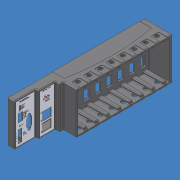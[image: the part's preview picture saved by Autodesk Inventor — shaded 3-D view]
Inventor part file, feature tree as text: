
AUTODESK INVENTOR PART (.ipt)
format: ipt  version: 2011 (Build 150239000, 239)  size: 1,395,712 bytes
history: native  units: mm (DEFAULTED — no unit token found)
features: sketch x25, extrude x19, pattern_linear x9, fillet x7, hole x4, mirror x2, other x2
ambient origin geometry x8: Origin, YZ Plane, XZ Plane, XY Plane, X Axis, Y Axis, Z Axis, Center Point
bodies: Solid1 (feature_tree)
feature tree (68):
  extrude  "Extrusion1"  Depth=15.494mm
  extrude  "Extrusion2"  Depth=58.928mm
  extrude  "Extrusion3"  Depth=44.45mm
  extrude  "Extrusion4"  Depth=34.29mm
  extrude  "Extrusion5"  Depth=278.8412mm
  hole  "Hole2"  [1 undecoded]
  mirror  "Mirror2"
  pattern_linear  "Rectangular Pattern1"  Count1=2 Spacing1=93.0148mm
  pattern_linear  "Rectangular Pattern2"  Count1=2 Spacing1=140.589mm
  pattern_linear  "Rectangular Pattern3"  Count1=2 Spacing1=235.077mm
  pattern_linear  "Rectangular Pattern5"  Count1=2 Spacing1=81.534mm
  hole  "Hole3"  [1 undecoded]
  extrude  "Extrusion6"  Depth=11.1125mm
  extrude  "Extrusion7"  Depth=15.875mm
  extrude  "Extrusion8"  Depth=9.8298mm
  pattern_linear  "Rectangular Pattern6"  Count1=2 Spacing1=165.1mm
  extrude  "Extrusion9"  Depth=20.32mm
  pattern_linear  "Rectangular Pattern7"  Spacing1=5.08mm  [1 undecoded]
  extrude  "Extrusion10"  Depth=6.35mm
  extrude  "Extrusion11"  Depth=1.905mm
  extrude  "Extrusion12"  Depth=3.175mm TaperAngle=0.0deg
  extrude  "Extrusion13"  Depth=80.0mm
  extrude  "Extrusion14"  Depth=83.058mm
  pattern_linear  "Rectangular Pattern8"  Spacing1=39.624mm  [1 undecoded]
  extrude  "Extrusion15"  Depth=0.508mm TaperAngle=0.0deg
  fillet  "Fillet1"  Radius=83.058mm
  fillet  "Fillet4"  Radius=30.48mm
  extrude  "Extrusion19"  Depth=0.508mm TaperAngle=0.0deg
  extrude  "Extrusion16"  Depth=39.37mm
  extrude  "Extrusion17"  Depth=41.275mm
  fillet  "Fillet2"  Radius=6.35mm
  hole  "Hole4"  [1 undecoded]
  pattern_linear  "Rectangular Pattern9"  Spacing1=9.525mm  [1 undecoded]
  mirror  "Mirror4"
  extrude  "Extrusion18"  Depth=18.034mm
  fillet  "Fillet3"  Radius=17.272mm
  pattern_linear  "Rectangular Pattern10"  Spacing1=5.715mm  [1 undecoded]
  hole  "Hole5"  [1 undecoded]
  fillet  "Fillet5"  Radius=20.0mm
  fillet  "Fillet7"  Radius=16.6116mm
  fillet  "Fillet8"  Radius=9.6774mm
  sketch  "Sketch1"  dims[d0=286.512mm d1=15.494mm]
  sketch  "Sketch2"  dims[d2=86.36mm d3=58.928mm]
  sketch  "Sketch3"  dims[d4=88.138mm d5=0.0mm d6=44.45mm]
  sketch  "Sketch4"  dims[d7=6.096mm d8=34.29mm]
  sketch  "Sketch6"  dims[d9=9.525mm d10=278.8412mm]
  sketch  "Sketch7"  dims[d11=80.4672mm d12=2.159mm d13=0.0mm]
  sketch  "Sketch8"  dims[d14=77.6732mm]
  sketch  "Sketch9"  dims[d15=276.0472mm]
  sketch  "Sketch10"  dims[d16=10.795mm d17=0.0mm]
  sketch  "Sketch11"  dims[d18=80.264mm]
  sketch  "Sketch12"  dims[d19=6.35mm]
  sketch  "Sketch13"  dims[d20=191.262mm]
  sketch  "Sketch14"  dims[d21=43.18mm d22=0.0mm]
  sketch  "Sketch15"  dims[d32=7.62mm]
  sketch  "Sketch16"  dims[d33=4.9149mm]
  sketch  "Sketch17"  dims[d34=11.6586mm]
  sketch  "Sketch18"  dims[d35=5.842mm d36=0.0mm]
  sketch  "Sketch19"  dims[d37=3.1242mm d38=12.7mm d39=9.525mm d40=6.35mm d41=14.3117mm d42=19.05mm d43=20.594885mm d44=20.0mm d46=93.0148mm d47=20.0mm d49=140.589mm d50=20.0mm d52=235.077mm d56=20.0mm d58=81.534mm]
  sketch  "Sketch20"  dims[d59=26.2636mm d60=59.055mm]
  sketch  "Sketch21"  dims[d61=165.1mm]
  sketch  "Sketch22"  dims[d62=5.334mm d63=12.7mm d64=9.525mm d65=6.35mm d66=14.3117mm d67=19.05mm d68=20.594885mm d69=11.1125mm]
  sketch  "Sketch23"  dims[d70=2.54mm d71=0.0mm d72=15.875mm]
  sketch  "Sketch25"  dims[d73=3.175mm d74=0.0mm d75=9.8298mm]
  sketch  "Sketch26"  dims[d76=3.175mm d77=0.0mm d78=20.0mm d80=165.1mm]
  sketch  "Sketch27"  dims[d81=11.0998mm d82=20.32mm d83=5.08mm d84=6.35mm d85=1.905mm d86=3.175mm d87=0.0mm d88=80.0mm d90=23.622mm d91=83.058mm d92=39.624mm d93=0.508mm d94=0.0mm d95=83.058mm d96=30.48mm d97=0.508mm d98=0.0mm d99=39.37mm d100=41.275mm d101=6.35mm d102=0.0mm d103=5.08mm d104=9.525mm d105=0.0mm d106=18.034mm d107=17.272mm d108=5.715mm d109=9.525mm d110=0.0mm d111=20.0mm d113=20.32mm d114=16.6116mm d115=9.6774mm d116=8.001mm d117=25.1968mm d119=4.953mm d120=4.572mm d121=5.08mm d122=24.13mm d123=11.176mm d124=10.16mm d125=7.493mm d126=3.048mm d127=9.525mm d128=0.0mm d129=1.524mm d130=3.175mm d131=8.89mm d132=35.306mm d133=10.668mm d134=182.88mm d135=25.4mm d136=24.638mm d137=0.381mm d138=0.0mm d139=19.05mm d140=15.875mm d141=0.762mm d142=0.0mm d143=2.54mm d144=13.97mm d145=8.89mm d146=12.7mm d147=9.525mm d148=6.35mm d149=14.3117mm d150=6.35mm d151=20.594885mm d152=80.0mm d154=23.622mm d155=9.525mm d156=4.572mm d157=0.254mm d158=40.64mm d159=0.0mm d161=0.349066mm d162=6.35mm d163=1.27mm d164=80.0mm d166=23.622mm d167=38.608mm d168=14.732mm d169=24.892mm d170=43.942mm d171=62.992mm d172=2.6416mm d173=12.7mm d174=9.525mm d175=6.35mm d176=14.3117mm d177=6.35mm d178=20.594885mm d179=6.096mm d180=31.242mm d181=25.4mm d182=17.272mm d183=3.048mm d195=3.175mm d196=20.32mm d197=17.453293mm d198=10.922mm d199=40.132mm d200=0.0mm d201=2.0066mm d203=1.27mm d204=0.508mm]
  other  "Image3"
  other  "Image4"
note: 8 required parameter values undecoded (feature->parameter linkage not recoverable at this tier; creation-order binding heuristic only, values carry confidence <= 0.55)
